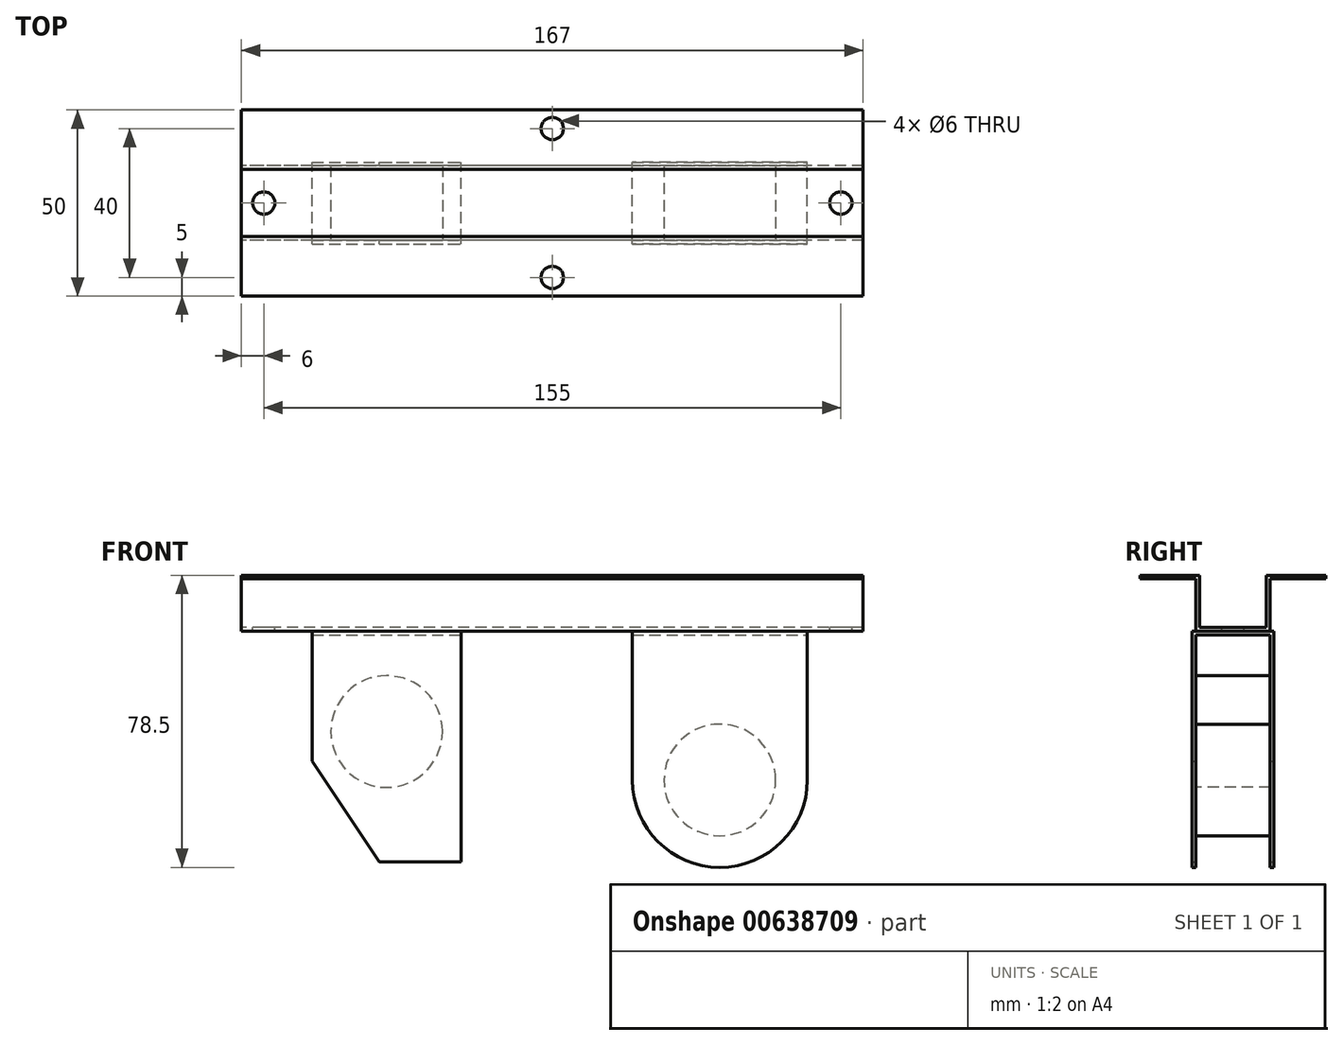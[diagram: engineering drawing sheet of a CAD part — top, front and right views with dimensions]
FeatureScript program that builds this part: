
annotation { "Feature Type Name" : "Feature", "Feature Type Description" : "" }
export const myFeature = defineFeature(function(context is Context, id is Id, definition is map)
    precondition{}
    {
        {
            var Q0;
            Q0=qCreatedBy(makeId("Right.planeOp"),FACE);
            var sketch = newSketch(context, id + "F0", { "sketchPlane" : qUnion([Q0])});
            skLineSegment(sketch, "E0", {"start": v(-25, 0) * mm, "end": v(-9, 0) * mm});
            skLineSegment(sketch, "E1", {"start": v(-9, 0) * mm, "end": v(-9, -14) * mm});
            skLineSegment(sketch, "E2", {"start": v(-9, -14) * mm, "end": v(0, -14) * mm});
            skLineSegment(sketch, "E3.0", {"start": v(-10, -15) * mm, "end": v(0, -15) * mm});
            skLineSegment(sketch, "E3.1", {"start": v(-10, -1) * mm, "end": v(-10, -15) * mm});
            skLineSegment(sketch, "E3.2", {"start": v(-25, -1) * mm, "end": v(-10, -1) * mm});
            skLineSegment(sketch, "E4", {"start": v(-25, 0) * mm, "end": v(-25, -1) * mm});
            skLineSegment(sketch, "E5.MirrorCS", {"start": v(25, 0) * mm, "end": v(25, -1) * mm});
            skLineSegment(sketch, "E6.MirrorCS", {"start": v(9, -14) * mm, "end": v(0, -14) * mm});
            skLineSegment(sketch, "E7.MirrorCS", {"start": v(9, 0) * mm, "end": v(9, -14) * mm});
            skLineSegment(sketch, "E8.MirrorCS", {"start": v(10, -15) * mm, "end": v(0, -15) * mm});
            skLineSegment(sketch, "E9.MirrorCS", {"start": v(25, -1) * mm, "end": v(10, -1) * mm});
            skLineSegment(sketch, "E10.MirrorCS", {"start": v(25, 0) * mm, "end": v(9, 0) * mm});
            skLineSegment(sketch, "E11.MirrorCS", {"start": v(10, -1) * mm, "end": v(10, -15) * mm});
            skSolve(sketch);
        }
        {
            var Q0;
            Q0 = qSketchRegion(id + "F0", true);
            extrude(context, id + "F1", {"entities" : qUnion([Q0]), "depth" : 167 * mm, "offsetDistance" : 25.4 * mm});
        }
        {
            var Q0;
            Q0=qCreatedBy(makeId("Front.planeOp"),FACE);
            var sketch = newSketch(context, id + "F2", { "sketchPlane" : qUnion([Q0])});
            skLineSegment(sketch, "E12.0", {"start": v(167, -15) * mm, "end": v(0, -15) * mm, "construction": true});
            skLineSegment(sketch, "E13.bottom", {"start": v(152, -15) * mm, "end": v(105, -15) * mm});
            skLineSegment(sketch, "E13.left", {"start": v(152, -15) * mm, "end": v(152, -55) * mm});
            skLineSegment(sketch, "E13.right", {"start": v(105, -15) * mm, "end": v(105, -55) * mm});
            skArc(sketch, "E14", {"start": v(105, -55) * mm, "mid": v(128.5, -78.5) * mm, "end": v(152, -55) * mm});
            skSolve(sketch);
        }
        {
            var Q0;
            Q0 = qSketchRegion(id + "F2", true);
            extrude(context, id + "F3", {"entities" : qUnion([Q0]), "operationType" : NewBodyOperationType.ADD, "endBound" : BoundingType.SYMMETRIC, "depth" : 22 * mm, "offsetDistance" : 25.4 * mm});
        }
        {
            var Q0;
            Q0=qCreatedBy(makeId("Front.planeOp"),FACE);
            var sketch = newSketch(context, id + "F4", { "sketchPlane" : qUnion([Q0])});
            skLineSegment(sketch, "E15.0", {"start": v(105, -15) * mm, "end": v(0, -15) * mm, "construction": true});
            skLineSegment(sketch, "E16.bottom", {"start": v(19, -15) * mm, "end": v(59, -15) * mm});
            skLineSegment(sketch, "E16.top", {"start": v(37, -77) * mm, "end": v(59, -77) * mm});
            skLineSegment(sketch, "E16.left", {"start": v(19, -15) * mm, "end": v(19, -50) * mm});
            skLineSegment(sketch, "E16.right", {"start": v(59, -15) * mm, "end": v(59, -77) * mm});
            skLineSegment(sketch, "E17", {"start": v(19, -50) * mm, "end": v(37, -77) * mm});
            skSolve(sketch);
        }
        {
            var Q0;
            Q0 = qSketchRegion(id + "F4", true);
            extrude(context, id + "F5", {"entities" : qUnion([Q0]), "operationType" : NewBodyOperationType.ADD, "endBound" : BoundingType.SYMMETRIC, "depth" : 22 * mm, "offsetDistance" : 25.4 * mm});
        }
        {
            var Q0;
            Q0=makeQuery(id+"F3.opExtrude","SWEPT_FACE",FACE,{"disambiguationData":[OSD([sQuery(id+"F2.wireOp",EDGE,"E13.left")])]});
            var sketch = newSketch(context, id + "F6", { "sketchPlane" : qUnion([Q0])});
            skLineSegment(sketch, "E18.bottom", {"start": v(-10, -16) * mm, "end": v(0, -16) * mm});
            skLineSegment(sketch, "E18.top", {"start": v(-10, -83.89) * mm, "end": v(0, -83.89) * mm});
            skLineSegment(sketch, "E18.left", {"start": v(-10, -16) * mm, "end": v(-10, -83.89) * mm});
            skLineSegment(sketch, "E19.MirrorCS", {"start": v(10, -16) * mm, "end": v(10, -83.89) * mm});
            skLineSegment(sketch, "E20.MirrorCS", {"start": v(10, -83.89) * mm, "end": v(0, -83.89) * mm});
            skLineSegment(sketch, "E21.MirrorCS", {"start": v(10, -16) * mm, "end": v(0, -16) * mm});
            skSolve(sketch);
        }
        {
            var Q0;
            Q0 = qSketchRegion(id + "F6", true);
            extrude(context, id + "F7", {"entities" : qUnion([Q0]), "operationType" : NewBodyOperationType.REMOVE, "endBound" : BoundingType.THROUGH_ALL, "oppositeDirection" : true, "depth" : 25.4 * mm, "offsetDistance" : 25.4 * mm});
        }
        {
            var Q0;
            Q0=makeQuery(id+"F1.opExtrude","SWEPT_FACE",FACE,{"disambiguationData":[OSD([sQuery(id+"F0.wireOp",EDGE,"E0")])]});
            var sketch = newSketch(context, id + "F8", { "sketchPlane" : qUnion([Q0])});
            skCircle(sketch, "E22", {"center": v(83.5, 20) * mm, "radius": 3 * mm});
            skCircle(sketch, "E23.MirrorC", {"center": v(83.5, -20) * mm, "radius": 3 * mm});
            skSolve(sketch);
        }
        {
            var Q0;
            Q0 = qSketchRegion(id + "F8", true);
            extrude(context, id + "F9", {"entities" : qUnion([Q0]), "operationType" : NewBodyOperationType.REMOVE, "endBound" : BoundingType.THROUGH_ALL, "oppositeDirection" : true, "depth" : 25.4 * mm, "offsetDistance" : 25.4 * mm});
        }
        {
            var Q0;
            Q0=makeQuery(id+"F1.opExtrude","SWEPT_FACE",FACE,{"disambiguationData":[OSD([sQuery(id+"F0.wireOp",EDGE,"E2"),sQuery(id+"F0.wireOp",EDGE,"E6.MirrorCS")])]});
            var sketch = newSketch(context, id + "F10", { "sketchPlane" : qUnion([Q0])});
            skCircle(sketch, "E24", {"center": v(161, 0) * mm, "radius": 3 * mm});
            skCircle(sketch, "E25", {"center": v(6, 0) * mm, "radius": 3 * mm});
            skSolve(sketch);
        }
        {
            var Q0;
            Q0 = qSketchRegion(id + "F10", true);
            extrude(context, id + "F11", {"entities" : qUnion([Q0]), "operationType" : NewBodyOperationType.REMOVE, "endBound" : BoundingType.THROUGH_ALL, "oppositeDirection" : true, "depth" : 25.4 * mm, "offsetDistance" : 25.4 * mm});
        }
        {
            var Q0;
            Q0=makeQuery(id+"F3.opExtrude","CAP_FACE",FACE,{"disambiguationData":[OSD([sQuery(id+"F2.wireOp",EDGE,"E13.bottom"),sQuery(id+"F2.wireOp",EDGE,"E13.left"),sQuery(id+"F2.wireOp",EDGE,"E13.right"),sQuery(id+"F2.wireOp",EDGE,"E14")])],"isStart":false});
            var sketch = newSketch(context, id + "F12", { "sketchPlane" : qUnion([Q0])});
            skCircle(sketch, "E26", {"center": v(128.5, -55) * mm, "radius": 15 * mm});
            skSolve(sketch);
        }
        {
            var Q0;
            Q0 = qSketchRegion(id + "F12", true);
            var Q1;
            Q1=makeQuery(id+"F7.boolean.opBoolean","COPY",FACE,{"disambiguationData":[TD([makeQuery(id+"F3.opExtrude","SWEPT_FACE",FACE,{"disambiguationData":[OSD([sQuery(id+"F2.wireOp",EDGE,"E13.left")])]})])],"derivedFrom":makeQuery(id+"F7.opExtrude","SWEPT_FACE",FACE,{"disambiguationData":[OSD([sQuery(id+"F6.wireOp",EDGE,"E19.MirrorCS")])]})});
            extrude(context, id + "F13", {"entities" : qUnion([Q0]), "operationType" : NewBodyOperationType.ADD, "endBound" : BoundingType.UP_TO_SURFACE, "oppositeDirection" : true, "depth" : 25.4 * mm, "endBoundEntityFace" : qUnion([Q1]), "offsetDistance" : 25.4 * mm});
        }
        {
            var Q0;
            Q0=makeQuery(id+"F5.opExtrude","CAP_FACE",FACE,{"disambiguationData":[OSD([sQuery(id+"F4.wireOp",EDGE,"E16.bottom"),sQuery(id+"F4.wireOp",EDGE,"E16.top"),sQuery(id+"F4.wireOp",EDGE,"E16.left"),sQuery(id+"F4.wireOp",EDGE,"E16.right"),sQuery(id+"F4.wireOp",EDGE,"E17")])],"isStart":false});
            var sketch = newSketch(context, id + "F14", { "sketchPlane" : qUnion([Q0])});
            skCircle(sketch, "E27", {"center": v(39, -42) * mm, "radius": 15 * mm});
            skSolve(sketch);
        }
        {
            var Q0;
            Q0 = qSketchRegion(id + "F14", true);
            var Q1;
            Q1=makeQuery(id+"F7.boolean.opBoolean","COPY",FACE,{"disambiguationData":[TD([makeQuery(id+"F5.opExtrude","SWEPT_FACE",FACE,{"disambiguationData":[OSD([sQuery(id+"F4.wireOp",EDGE,"E16.top")])]})])],"derivedFrom":makeQuery(id+"F7.opExtrude","SWEPT_FACE",FACE,{"disambiguationData":[OSD([sQuery(id+"F6.wireOp",EDGE,"E19.MirrorCS")])]})});
            extrude(context, id + "F15", {"entities" : qUnion([Q0]), "operationType" : NewBodyOperationType.ADD, "endBound" : BoundingType.UP_TO_SURFACE, "oppositeDirection" : true, "depth" : 25.4 * mm, "endBoundEntityFace" : qUnion([Q1]), "offsetDistance" : 25.4 * mm});
        }
    });
